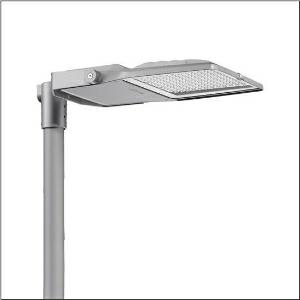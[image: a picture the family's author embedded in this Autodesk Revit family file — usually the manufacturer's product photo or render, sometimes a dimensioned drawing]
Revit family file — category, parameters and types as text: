
# Revit family: floodlight_fl_21_iq_midi___pl52_5xa7781f4d3a_7000
name_source: partatom
category: Lighting Fixtures
units: mm (PartAtom-declared; Revit-internal decimal feet)

## family parameters
Cut with Voids When Loaded = No
Host = Face
Light Source = No
Part Type = Normal
Room Calculation Point = No
Round Connector Dimension = Use Diameter
Shared = No

## types (1)
- --- (1 x LED, 37330 lm, 270.2 W, 4000K)
    Apparent Load = 270 VA
    CIE Flux Codes = 26 60 98 100 100
    Color Rendering = 70
    Color Temperature = 4000K
    Default Elevation = 1800 mm
    Description = Floodlight FL 21 iQ midi, floodlight, primary light control with lens, of PMMA, primary optical cover: protective disc, of toughened safety glass, transparent, light distribution: PL52, light emission: direct distribution, installation type: surface-mounted, lamps: LED, High Power LED, rated values: 37.330lm | 270,2W | 138,2lm/W (begin service life); end service life: 37.330lm | 286,6W; at 50% lumin. flux: 18.665lm | 117,7W | 158,6lm/W, colour temperature: 4000K, colour rendering: CRI > 70, light colour: 740, light setting 1 begin service life: 100% | 37.330lm | 270,2W | 138,2lm/W | 4.000K, light setting 1 end service life: 286,6W, further light settings possible, control: optimised constant luminous flux control (CLO 2.0), Desk-Remote (wireless, voltage-free reading and setting of iQ features in the workshop via application-optimized NFC function/RFID function), Light-Fading, Smart-Wire, Night-Set, Lumen-Switch, Temp-Guard, Auto-Match, pre-setting: linear dimming characteristic, with terminal, 6-pole, mains connection: 220..240V, AC, 50/60Hz, luminaire housing, of diecast aluminium, powder-coated, SITECO metallic grey (DB 702S), corrosivity category C5 mid according to DIN EN ISO 12944suitable for swimming poolschlorine-resistant, sealing non-destructively replaceable, please order mast flange separately, mast bracket, of steel, galvanised, powder-coated, SITECO metallic grey (DB 702S), protection rating (complete): IP66, insulation class (complete): insulation class II (safety insulation), certification: CE, ENEC, VDE, protection symbol: D, impact resistance: IK08, permissible operating ambient temperature: -40..+40°C, permissible operating ambient temperature for outdoor applications: -40..+50°C, standard: DIN EN 12944, LABS conformity tested according to VDMA 24364:2018-05, packaging unit: 1 piece

Light Distribution: PL52
    Height = 76 mm
    Lamp = 1 x LED
    Lamp Light Flux = 37330 lm
    Lamp Power = 270.2 W
    Lamp count = 1
    Length = 657 mm
    Luminous efficacy = 138 lm/W
    Manufacturer = Siteco
    ModVariant = No
    Model = 5XA7781F4D3A
    Number of Poles = 1
    OnlyDefault = Yes
    Power Factor = 1
    Product Name = Floodlight FL 21 iQ midi | PL52
    Product group = floodlight | pylon annexe
    ProductGroupID = 6201
    Protection Class = Protection class II
    Protection Degree = IP 66
    RLX_Detail_Level = 1
    RLX_Emergency_Light_Flux = 0 lm
    RLX_Emergency_Type = 0
    RLX_Emergency_Type_DB = No
    RlxData = <blob elided: 154001 chars, md5=fb6a0c48>
    Socket = socket
    Standby Power = 0 W
    System Light Flux = 37330 lm
    System Power = 270 W
    Type Comments = factory setting: luminous flux: 100 % | dim-lin: 254 | 620 mA
    Type Image = l_1007123.jpg
    URL = http://relux.com
    VarID = @adj_105695
    Voltage = 0 V
    Weight = 0.00 kg
    Width = 442 mm

## geometry (parser evidence)
native form markers: Blend x4, Sweep x15
no freeform markers — native parametric forms only
